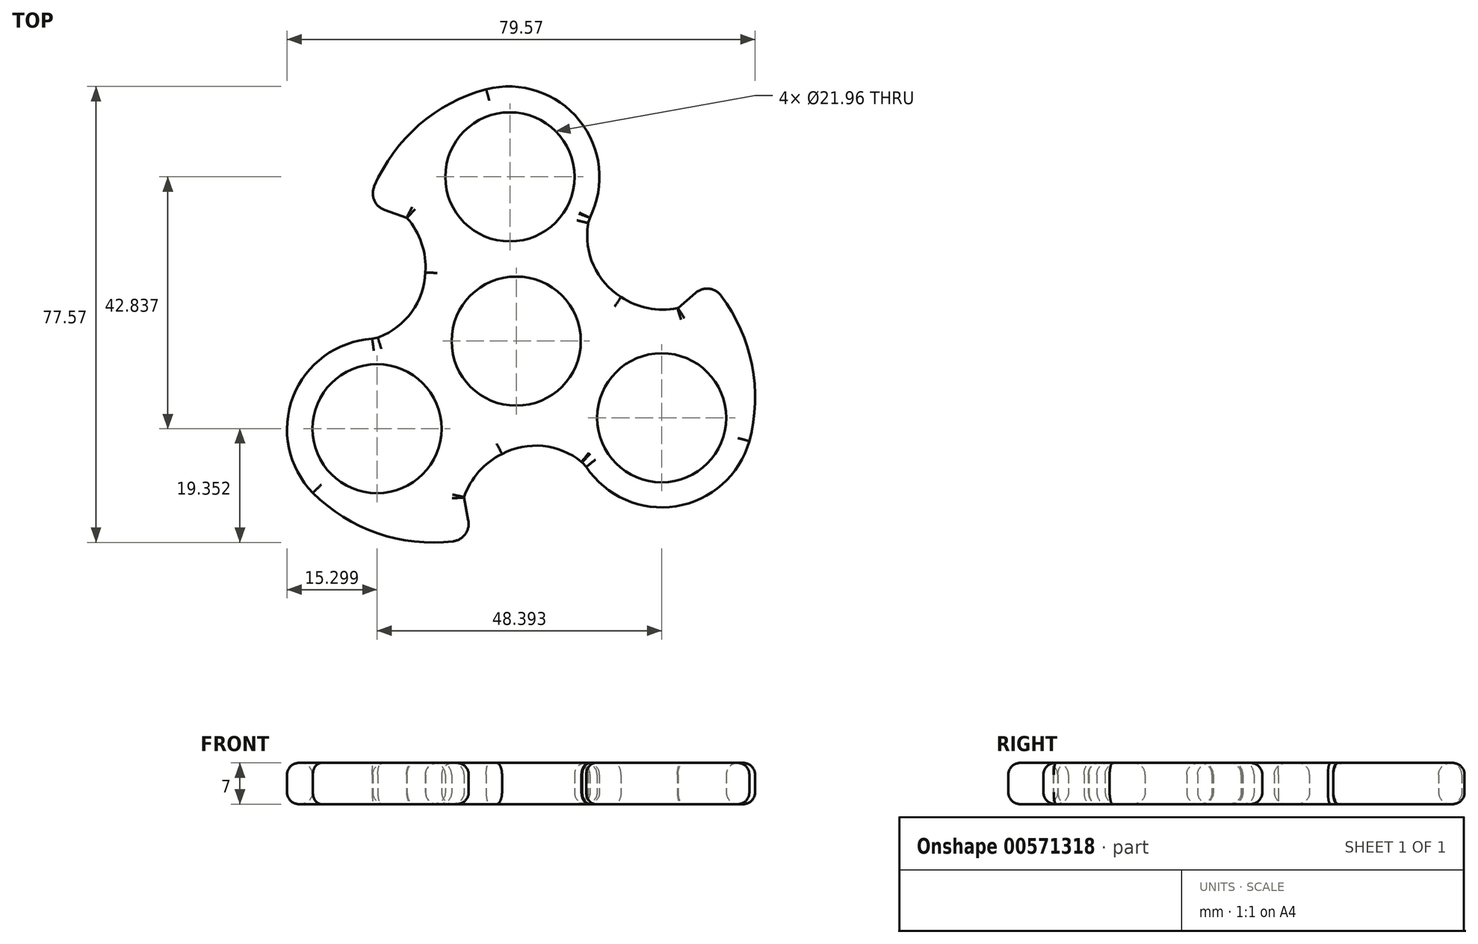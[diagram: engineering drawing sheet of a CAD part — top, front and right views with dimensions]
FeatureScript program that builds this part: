
annotation { "Feature Type Name" : "Feature", "Feature Type Description" : "" }
export const myFeature = defineFeature(function(context is Context, id is Id, definition is map)
    precondition{}
    {
        {
            var Q0;
            Q0=qCreatedBy(makeId("Top.planeOp"),FACE);
            var sketch = newSketch(context, id + "F0", { "sketchPlane" : qUnion([Q0])});
            skCircle(sketch, "E0", {"center": v(0, 0) * mm, "radius": 10.98 * mm});
            skCircle(sketch, "E1", {"center": v(-1.07, 27.94) * mm, "radius": 10.98 * mm});
            skPoint(sketch, "E2.start.orphan", {"position": v(0, 43.22) * mm});
            skPoint(sketch, "E3.2.0.end.orphan", {"position": v(32.77, 10.17) * mm});
            skPoint(sketch, "E4.orphan", {"position": v(11.11, -20.52) * mm});
            skPoint(sketch, "E5.trimOffspring.end.orphan", {"position": v(27.48, 5.59) * mm});
            skPoint(sketch, "E6.orphan", {"position": v(-8.9, -26.47) * mm});
            skPoint(sketch, "E7.orphan", {"position": v(-18.61, 21.02) * mm});
            skPoint(sketch, "E8.2.0", {"position": v(-23.33, 0.64) * mm});
            skArc(sketch, "E8.2.2", {"start": v(-23.36, 0.67) * mm, "mid": v(-17.74, 4.99) * mm, "end": v(-15.44, 11.7) * mm});
            skArc(sketch, "E8.2.3", {"start": v(-15.44, 11.7) * mm, "mid": v(-16.08, 16.63) * mm, "end": v(-18.56, 20.95) * mm});
            skLineSegment(sketch, "E8.2.4", {"start": v(-18.64, 21) * mm, "end": v(-25.23, 23.3) * mm});
            skLineSegment(sketch, "E8.2.5", {"start": v(-18.56, 20.95) * mm, "end": v(-18.64, 21) * mm});
            skArc(sketch, "E8.2.6", {"start": v(-5.1, 42.84) * mm, "mid": v(-17.7, 35.68) * mm, "end": v(-25.23, 23.3) * mm});
            skArc(sketch, "E8.2.7", {"start": v(12.54, 21) * mm, "mid": v(10.72, 37.58) * mm, "end": v(-5.1, 42.84) * mm});
            skPoint(sketch, "E9.orphan", {"position": v(12.77, 20.88) * mm});
            skPoint(sketch, "E10.1.3.end.orphan", {"position": v(-7.57, -33.47) * mm});
            skPoint(sketch, "E11.center", {"position": v(-0.02, -0.02) * mm});
            skPoint(sketch, "E12.orphan", {"position": v(12.23, 19.85) * mm});
            skPoint(sketch, "E13.orphan", {"position": v(32.77, 10.14) * mm});
            skLineSegment(sketch, "E14", {"start": v(-23.36, 0.67) * mm, "end": v(-23.52, 0.6) * mm});
            skPoint(sketch, "E15.orphan", {"position": v(-23.37, 0.63) * mm});
            skArc(sketch, "E16.1.2", {"start": v(11.1, -20.55) * mm, "mid": v(4.55, -17.84) * mm, "end": v(-2.4, -19.2) * mm});
            skArc(sketch, "E16.1.3", {"start": v(-2.4, -19.2) * mm, "mid": v(-6.36, -22.22) * mm, "end": v(-8.86, -26.52) * mm});
            skLineSegment(sketch, "E16.1.4", {"start": v(-8.87, -26.62) * mm, "end": v(-7.57, -33.48) * mm});
            skArc(sketch, "E16.1.5", {"start": v(-34.57, -25.8) * mm, "mid": v(-22.07, -33.15) * mm, "end": v(-7.57, -33.48) * mm});
            skArc(sketch, "E16.1.6", {"start": v(-24.49, 0.39) * mm, "mid": v(-37.93, -9.48) * mm, "end": v(-34.57, -25.8) * mm});
            skLineSegment(sketch, "E16.1.7", {"start": v(-24.49, 0.39) * mm, "end": v(-23.52, 0.6) * mm});
            skLineSegment(sketch, "E16.2.0", {"start": v(12.53, 20.98) * mm, "end": v(12.25, 20.09) * mm});
            skLineSegment(sketch, "E16.2.1", {"start": v(12.22, 19.9) * mm, "end": v(12.25, 20.09) * mm});
            skArc(sketch, "E16.2.2", {"start": v(12.22, 19.9) * mm, "mid": v(13.15, 12.87) * mm, "end": v(17.81, 7.52) * mm});
            skArc(sketch, "E16.2.3", {"start": v(17.81, 7.52) * mm, "mid": v(22.41, 5.6) * mm, "end": v(27.4, 5.59) * mm});
            skLineSegment(sketch, "E16.2.4", {"start": v(27.5, 5.63) * mm, "end": v(32.78, 10.18) * mm});
            skArc(sketch, "E16.2.5", {"start": v(39.63, -17.01) * mm, "mid": v(39.73, -2.53) * mm, "end": v(32.78, 10.18) * mm});
            skArc(sketch, "E16.2.6", {"start": v(11.9, -21.38) * mm, "mid": v(27.17, -28.09) * mm, "end": v(39.63, -17.01) * mm});
            skLineSegment(sketch, "E16.2.7", {"start": v(11.9, -21.38) * mm, "end": v(11.22, -20.63) * mm});
            skPoint(sketch, "E17.orphan", {"position": v(12.22, 19.89) * mm});
            skLineSegment(sketch, "E18", {"start": v(12.54, 21) * mm, "end": v(12.53, 20.98) * mm});
            skPoint(sketch, "E19.orphan", {"position": v(12.55, 21.05) * mm});
            skLineSegment(sketch, "E20", {"start": v(11.1, -20.55) * mm, "end": v(11.22, -20.63) * mm});
            skPoint(sketch, "E21.orphan", {"position": v(10.91, -20.39) * mm});
            skPoint(sketch, "E22.orphan", {"position": v(-23.11, 0.75) * mm});
            skPoint(sketch, "E23.orphan", {"position": v(-23.54, 0.6) * mm});
            skLineSegment(sketch, "E24", {"start": v(-8.86, -26.52) * mm, "end": v(-8.87, -26.62) * mm});
            skLineSegment(sketch, "E25", {"start": v(27.4, 5.59) * mm, "end": v(27.5, 5.63) * mm});
            skCircle(sketch, "E26.1.0", {"center": v(-23.66, -14.9) * mm, "radius": 10.98 * mm});
            skCircle(sketch, "E26.2.0", {"center": v(24.73, -13.04) * mm, "radius": 10.98 * mm});
            skSolve(sketch);
        }
        {
            var Q0;
            Q0=qSketchRegion(id+"F0",true);
            extrude(context, id + "F1", {"entities" : qUnion([Q0]), "depth" : 7 * mm, "offsetDistance" : 25 * mm});
        }
        {
            var Q0;
            Q0=makeQuery(id+"F1.opExtrude","CAP_FACE",FACE,{"disambiguationData":[OSD([sQuery(id+"F0.wireOp",EDGE,"E0"),sQuery(id+"F0.wireOp",EDGE,"E1"),sQuery(id+"F0.wireOp",EDGE,"bfb47979-994e-4c35-8f3f-2d9462ef9953.1.0"),sQuery(id+"F0.wireOp",EDGE,"bfb47979-994e-4c35-8f3f-2d9462ef9953.2.0"),sQuery(id+"F0.wireOp",EDGE,"E10.1.0"),sQuery(id+"F0.wireOp",EDGE,"E10.1.1"),sQuery(id+"F0.wireOp",EDGE,"E10.1.2"),sQuery(id+"F0.wireOp",EDGE,"E10.1.3"),sQuery(id+"F0.wireOp",EDGE,"E10.1.4"),sQuery(id+"F0.wireOp",EDGE,"MSOVAvHY-2dng-qJIN-EstG-JEKkyfnc06y0"),sQuery(id+"F0.wireOp",EDGE,"Qhv8092y-Y5Qe-Pu52-p0u7-aBsJBwILmqKw"),sQuery(id+"F0.wireOp",EDGE,"E8.1.2"),sQuery(id+"F0.wireOp",EDGE,"E8.1.3"),sQuery(id+"F0.wireOp",EDGE,"E8.1.4"),sQuery(id+"F0.wireOp",EDGE,"E8.1.5"),sQuery(id+"F0.wireOp",EDGE,"E8.1.6"),sQuery(id+"F0.wireOp",EDGE,"E8.1.7"),sQuery(id+"F0.wireOp",EDGE,"E8.1.8"),sQuery(id+"F0.wireOp",EDGE,"E8.2.2"),sQuery(id+"F0.wireOp",EDGE,"E8.2.3"),sQuery(id+"F0.wireOp",EDGE,"E8.2.4"),sQuery(id+"F0.wireOp",EDGE,"E8.2.5"),sQuery(id+"F0.wireOp",EDGE,"E8.2.6"),sQuery(id+"F0.wireOp",EDGE,"E8.2.7"),sQuery(id+"F0.wireOp",EDGE,"E8.2.8")])],"isStart":false});
            var Q1;
            Q1=makeQuery(id+"F1.opExtrude","CAP_FACE",FACE,{"disambiguationData":[OSD([sQuery(id+"F0.wireOp",EDGE,"E0"),sQuery(id+"F0.wireOp",EDGE,"E1"),sQuery(id+"F0.wireOp",EDGE,"bfb47979-994e-4c35-8f3f-2d9462ef9953.1.0"),sQuery(id+"F0.wireOp",EDGE,"bfb47979-994e-4c35-8f3f-2d9462ef9953.2.0"),sQuery(id+"F0.wireOp",EDGE,"E8.1.5"),sQuery(id+"F0.wireOp",EDGE,"E8.2.2"),sQuery(id+"F0.wireOp",EDGE,"E8.2.3"),sQuery(id+"F0.wireOp",EDGE,"E8.2.4"),sQuery(id+"F0.wireOp",EDGE,"E8.2.5"),sQuery(id+"F0.wireOp",EDGE,"E8.2.6"),sQuery(id+"F0.wireOp",EDGE,"E8.2.7"),sQuery(id+"F0.wireOp",EDGE,"wI4vbt6F-0did-M85L-NOSj-vaBcgqnXykCr"),sQuery(id+"F0.wireOp",EDGE,"E11.1.0"),sQuery(id+"F0.wireOp",EDGE,"E11.1.1"),sQuery(id+"F0.wireOp",EDGE,"E11.1.2"),sQuery(id+"F0.wireOp",EDGE,"E11.1.3"),sQuery(id+"F0.wireOp",EDGE,"E11.1.4"),sQuery(id+"F0.wireOp",EDGE,"E11.1.5"),sQuery(id+"F0.wireOp",EDGE,"E11.2.0"),sQuery(id+"F0.wireOp",EDGE,"E11.2.1"),sQuery(id+"F0.wireOp",EDGE,"E11.2.2"),sQuery(id+"F0.wireOp",EDGE,"E11.2.3"),sQuery(id+"F0.wireOp",EDGE,"E11.2.4"),sQuery(id+"F0.wireOp",EDGE,"E11.2.5"),sQuery(id+"F0.wireOp",EDGE,"rdTHZh58-hr0x-KPgI-GlKq-AtTTfWVPiPXA")])],"isStart":true});
            fillet(context, id + "F2", {"entities" : qUnion([Q0, Q1]), "radius" : 2 * mm, "tangentPropagation" : true, "allowEdgeOverflow" : false});
        }
        {
            var Q0;
            Q0=makeQuery(id+"F1.opExtrude","SWEPT_EDGE",EDGE,{"disambiguationData":[OSD([sQuery(id+"F0.wireOp",EDGE,"E8.1.4"),sQuery(id+"F0.wireOp",EDGE,"E8.1.6")])]});
            var Q1;
            Q1=makeQuery(id+"F1.opExtrude","SWEPT_EDGE",EDGE,{"disambiguationData":[OSD([sQuery(id+"F0.wireOp",EDGE,"E8.2.4"),sQuery(id+"F0.wireOp",EDGE,"E8.2.6")])]});
            var Q2;
            Q2=makeQuery(id+"F1.opExtrude","SWEPT_EDGE",EDGE,{"disambiguationData":[OSD([sQuery(id+"F0.wireOp",EDGE,"E10.1.2"),sQuery(id+"F0.wireOp",EDGE,"E10.1.3")])]});
            var Q3;
            Q3=makeQuery(id+"F1.opExtrude","SWEPT_EDGE",EDGE,{"disambiguationData":[OSD([sQuery(id+"F0.wireOp",EDGE,"E11.2.2"),sQuery(id+"F0.wireOp",EDGE,"E11.2.3")])]});
            var Q4;
            Q4=makeQuery(id+"F1.opExtrude","SWEPT_EDGE",EDGE,{"disambiguationData":[OSD([sQuery(id+"F0.wireOp",EDGE,"E11.1.2"),sQuery(id+"F0.wireOp",EDGE,"E11.1.3")])]});
            var Q5;
            Q5=makeQuery(id+"F1.opExtrude","SWEPT_EDGE",EDGE,{"disambiguationData":[OSD([sQuery(id+"F0.wireOp",EDGE,"E16.2.4"),sQuery(id+"F0.wireOp",EDGE,"E16.2.5")])]});
            var Q6;
            Q6=makeQuery(id+"F1.opExtrude","SWEPT_EDGE",EDGE,{"disambiguationData":[OSD([sQuery(id+"F0.wireOp",EDGE,"E16.1.4"),sQuery(id+"F0.wireOp",EDGE,"E16.1.5")])]});
            fillet(context, id + "F3", {"entities" : qUnion([Q0, Q1, Q2, Q3, Q4, Q5, Q6]), "radius" : 3 * mm, "tangentPropagation" : true, "allowEdgeOverflow" : false});
        }
    });
